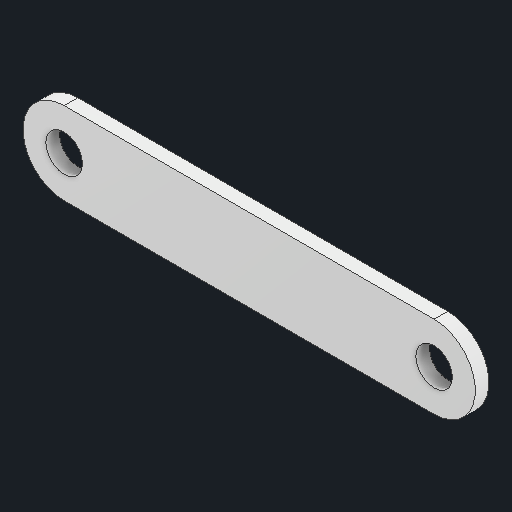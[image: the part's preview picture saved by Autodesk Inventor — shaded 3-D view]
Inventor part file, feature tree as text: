
AUTODESK INVENTOR PART (.ipt)
format: ipt  version: 2025 (Build 290162000, 162)  size: 96,256 bytes
history: native  units: in
note: dims shown in document units (in); Inventor stores cm internally (conversion verified against a paired STEP export)
features: extrude x1, sketch x1
ambient origin geometry x8: Origin, YZ Plane, XZ Plane, XY Plane, X Axis, Y Axis, Z Axis, Center Point
bodies: Solid1 (feature_tree)
feature tree (2):
  extrude  "Extrusion1"  Depth=0.0625in
  sketch  "Sketch1"  dims[d0=0.167in d1=0.167in d2=0.0625in d3=0.0in]
